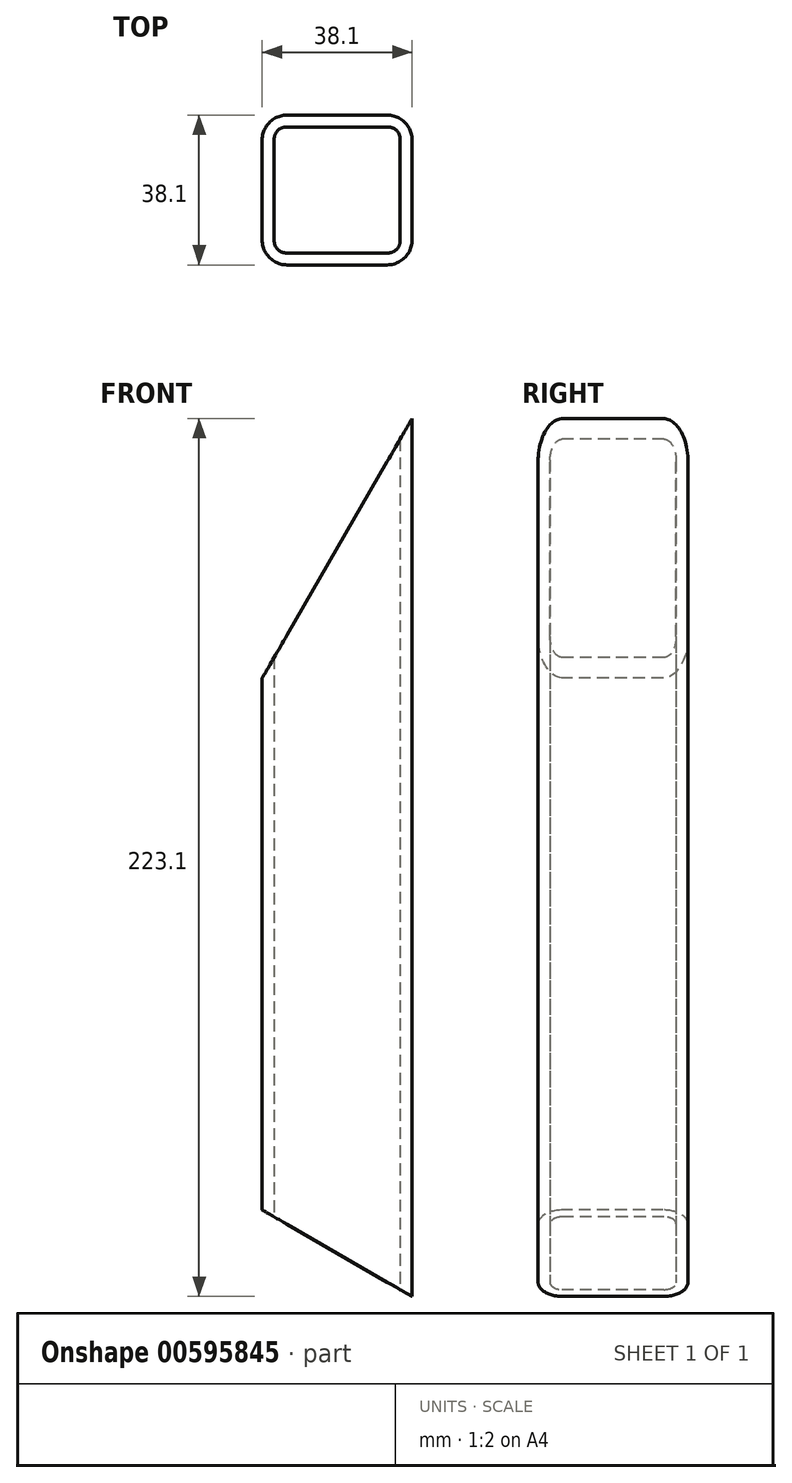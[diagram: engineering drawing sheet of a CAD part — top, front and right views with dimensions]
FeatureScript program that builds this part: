
annotation { "Feature Type Name" : "Feature", "Feature Type Description" : "" }
export const myFeature = defineFeature(function(context is Context, id is Id, definition is map)
    precondition{}
    {
        {
            var Q0;
            Q0=qCreatedBy(makeId("Top.planeOp"),FACE);
            var sketch = newSketch(context, id + "F0", { "sketchPlane" : qUnion([Q0])});
            skLineSegment(sketch, "E0.bottom", {"start": v(19.05, -19.05) * mm, "end": v(-19.05, -19.05) * mm});
            skLineSegment(sketch, "E0.top", {"start": v(19.05, 19.05) * mm, "end": v(-19.05, 19.05) * mm});
            skLineSegment(sketch, "E0.left", {"start": v(19.05, -19.05) * mm, "end": v(19.05, 19.05) * mm});
            skLineSegment(sketch, "E0.right", {"start": v(-19.05, -19.05) * mm, "end": v(-19.05, 19.05) * mm});
            skPoint(sketch, "E0.middle", {"position": v(0, 0) * mm});
            skLineSegment(sketch, "E1.bottom", {"start": v(-16, 16) * mm, "end": v(16, 16) * mm});
            skLineSegment(sketch, "E1.top", {"start": v(-16, -16) * mm, "end": v(16, -16) * mm});
            skLineSegment(sketch, "E1.left", {"start": v(-16, 16) * mm, "end": v(-16, -16) * mm});
            skLineSegment(sketch, "E1.right", {"start": v(16, 16) * mm, "end": v(16, -16) * mm});
            skSolve(sketch);
        }
        {
            var Q0;
            Q0=qSketchRegion(id+"F0",true);
            extrude(context, id + "F1", {"entities" : qUnion([Q0]), "depth" : 228.6 * mm, "offsetDistance" : 25.4 * mm});
        }
        {
            var Q0;
            Q0=makeQuery(id+"F1.opExtrude","SWEPT_EDGE",EDGE,{"disambiguationData":[OSD([sQuery(id+"F0.wireOp",EDGE,"E1.bottom"),sQuery(id+"F0.wireOp",EDGE,"E1.right")])]});
            var Q1;
            Q1=makeQuery(id+"F1.opExtrude","SWEPT_EDGE",EDGE,{"disambiguationData":[OSD([sQuery(id+"F0.wireOp",EDGE,"E1.bottom"),sQuery(id+"F0.wireOp",EDGE,"E1.left")])]});
            var Q2;
            Q2=makeQuery(id+"F1.opExtrude","SWEPT_EDGE",EDGE,{"disambiguationData":[OSD([sQuery(id+"F0.wireOp",EDGE,"E1.top"),sQuery(id+"F0.wireOp",EDGE,"E1.left")])]});
            var Q3;
            Q3=makeQuery(id+"F1.opExtrude","SWEPT_EDGE",EDGE,{"disambiguationData":[OSD([sQuery(id+"F0.wireOp",EDGE,"E1.top"),sQuery(id+"F0.wireOp",EDGE,"E1.right")])]});
            fillet(context, id + "F2", {"entities" : qUnion([Q0, Q1, Q2, Q3]), "radius" : 3.05 * mm, "tangentPropagation" : true, "allowEdgeOverflow" : false});
        }
        {
            var Q0;
            Q0=makeQuery(id+"F1.opExtrude","SWEPT_EDGE",EDGE,{"disambiguationData":[OSD([sQuery(id+"F0.wireOp",EDGE,"E0.top"),sQuery(id+"F0.wireOp",EDGE,"E0.right")])]});
            var Q1;
            Q1=makeQuery(id+"F1.opExtrude","SWEPT_EDGE",EDGE,{"disambiguationData":[OSD([sQuery(id+"F0.wireOp",EDGE,"E0.bottom"),sQuery(id+"F0.wireOp",EDGE,"E0.right")])]});
            var Q2;
            Q2=makeQuery(id+"F1.opExtrude","SWEPT_EDGE",EDGE,{"disambiguationData":[OSD([sQuery(id+"F0.wireOp",EDGE,"E0.bottom"),sQuery(id+"F0.wireOp",EDGE,"E0.left")])]});
            var Q3;
            Q3=makeQuery(id+"F1.opExtrude","SWEPT_EDGE",EDGE,{"disambiguationData":[OSD([sQuery(id+"F0.wireOp",EDGE,"E0.top"),sQuery(id+"F0.wireOp",EDGE,"E0.left")])]});
            fillet(context, id + "F3", {"entities" : qUnion([Q0, Q1, Q2, Q3]), "radius" : 6.35 * mm, "tangentPropagation" : true, "allowEdgeOverflow" : false});
        }
        {
            var Q0;
            Q0=qCreatedBy(makeId("Front.planeOp"),FACE);
            var sketch = newSketch(context, id + "F4", { "sketchPlane" : qUnion([Q0])});
            skLineSegment(sketch, "E2", {"start": v(19.05, 228.6) * mm, "end": v(-19.05, 162.6) * mm});
            skLineSegment(sketch, "E3", {"start": v(-19.05, 162.6) * mm, "end": v(-19.05, 228.6) * mm});
            skLineSegment(sketch, "E4", {"start": v(-19.05, 228.6) * mm, "end": v(19.05, 228.6) * mm});
            skLineSegment(sketch, "E5", {"start": v(19.05, 228.6) * mm, "end": v(19.05, 228.6) * mm});
            skSolve(sketch);
        }
        {
            var Q0;
            Q0=qSketchRegion(id+"F4",true);
            extrude(context, id + "F5", {"entities" : qUnion([Q0]), "operationType" : NewBodyOperationType.REMOVE, "endBound" : BoundingType.THROUGH_ALL, "oppositeDirection" : true, "depth" : 25.4 * mm, "offsetDistance" : 25.4 * mm, "hasSecondDirection" : true, "secondDirectionBound" : SecondDirectionBoundingType.THROUGH_ALL, "secondDirectionOppositeDirection" : false, "secondDirectionDepth" : 25.4 * mm});
        }
        {
            var Q0;
            Q0=qCreatedBy(makeId("Front.planeOp"),FACE);
            var sketch = newSketch(context, id + "F6", { "sketchPlane" : qUnion([Q0])});
            skLineSegment(sketch, "E6", {"start": v(-19.05, 0) * mm, "end": v(28.58, 0) * mm});
            skLineSegment(sketch, "E7", {"start": v(28.58, 0) * mm, "end": v(-19.05, 27.5) * mm});
            skLineSegment(sketch, "E8", {"start": v(-19.05, 27.5) * mm, "end": v(-19.05, 0) * mm});
            skSolve(sketch);
        }
        {
            var Q0;
            Q0=qSketchRegion(id+"F6",true);
            extrude(context, id + "F7", {"entities" : qUnion([Q0]), "operationType" : NewBodyOperationType.REMOVE, "endBound" : BoundingType.THROUGH_ALL, "oppositeDirection" : true, "depth" : 25.4 * mm, "offsetDistance" : 25.4 * mm, "hasSecondDirection" : true, "secondDirectionBound" : SecondDirectionBoundingType.THROUGH_ALL, "secondDirectionOppositeDirection" : false, "secondDirectionDepth" : 25.4 * mm});
        }
    });
